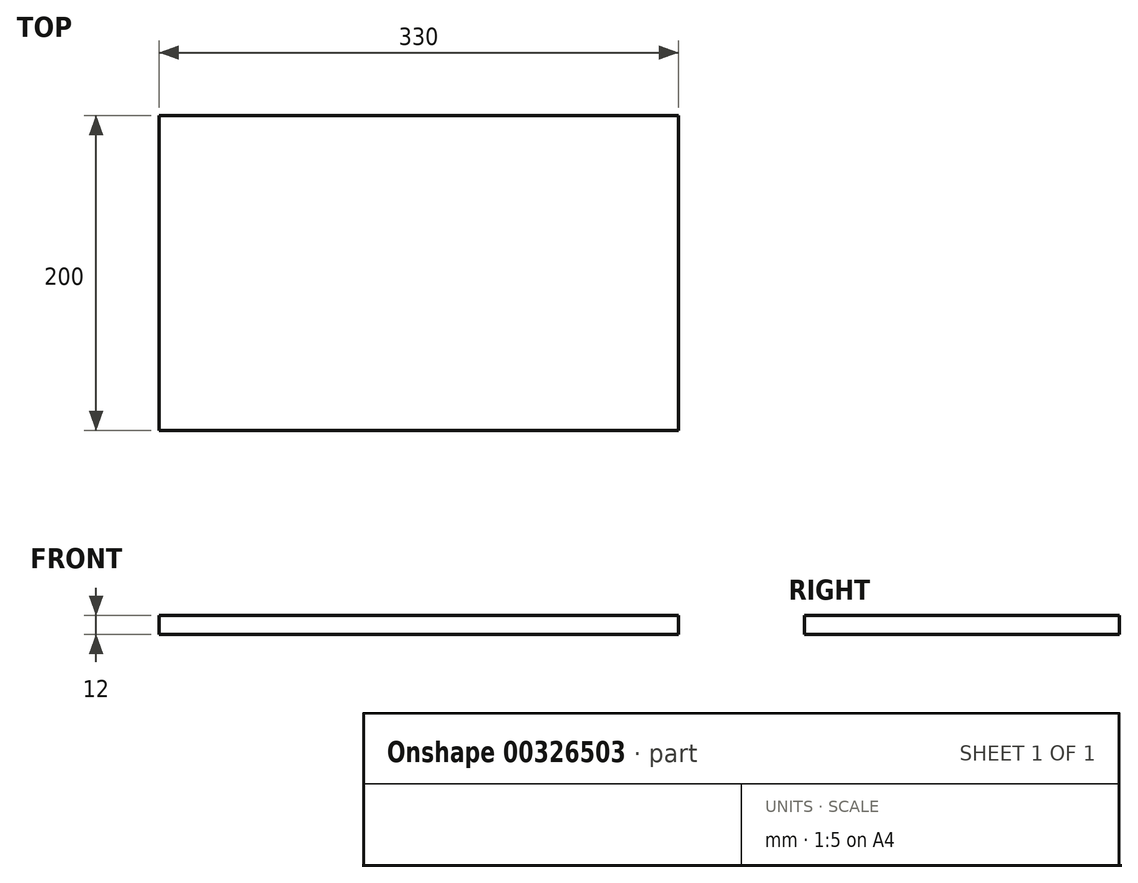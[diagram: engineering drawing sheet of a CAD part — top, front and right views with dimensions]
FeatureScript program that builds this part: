
annotation { "Feature Type Name" : "Feature", "Feature Type Description" : "" }
export const myFeature = defineFeature(function(context is Context, id is Id, definition is map)
    precondition{}
    {
        {
            var Q0;
            Q0=qCreatedBy(makeId("Top.planeOp"),FACE);
            var sketch = newSketch(context, id + "F0", { "sketchPlane" : qUnion([Q0])});
            skLineSegment(sketch, "E0", {"start": v(-135.69, -59.52) * mm, "end": v(194.31, -59.52) * mm});
            skLineSegment(sketch, "E1", {"start": v(194.31, -59.52) * mm, "end": v(194.31, 140.48) * mm});
            skLineSegment(sketch, "E2", {"start": v(194.31, 140.48) * mm, "end": v(-135.69, 140.48) * mm});
            skLineSegment(sketch, "E3", {"start": v(-135.69, 140.48) * mm, "end": v(-135.69, -59.52) * mm});
            skSolve(sketch);
        }
        {
            var Q0;
            Q0=makeQuery(id+"F0.imprint","IMPRINT",FACE,{"disambiguationData":[TD([[makeQuery(id+"F0.imprint","IMPRINT",EDGE,{"derivedFrom":sQuery(id+"F0.wireOp",EDGE,"E0")}),1.0]])]});
            extrude(context, id + "F1", {"entities" : qUnion([Q0]), "depth" : 12 * mm});
        }
    });
